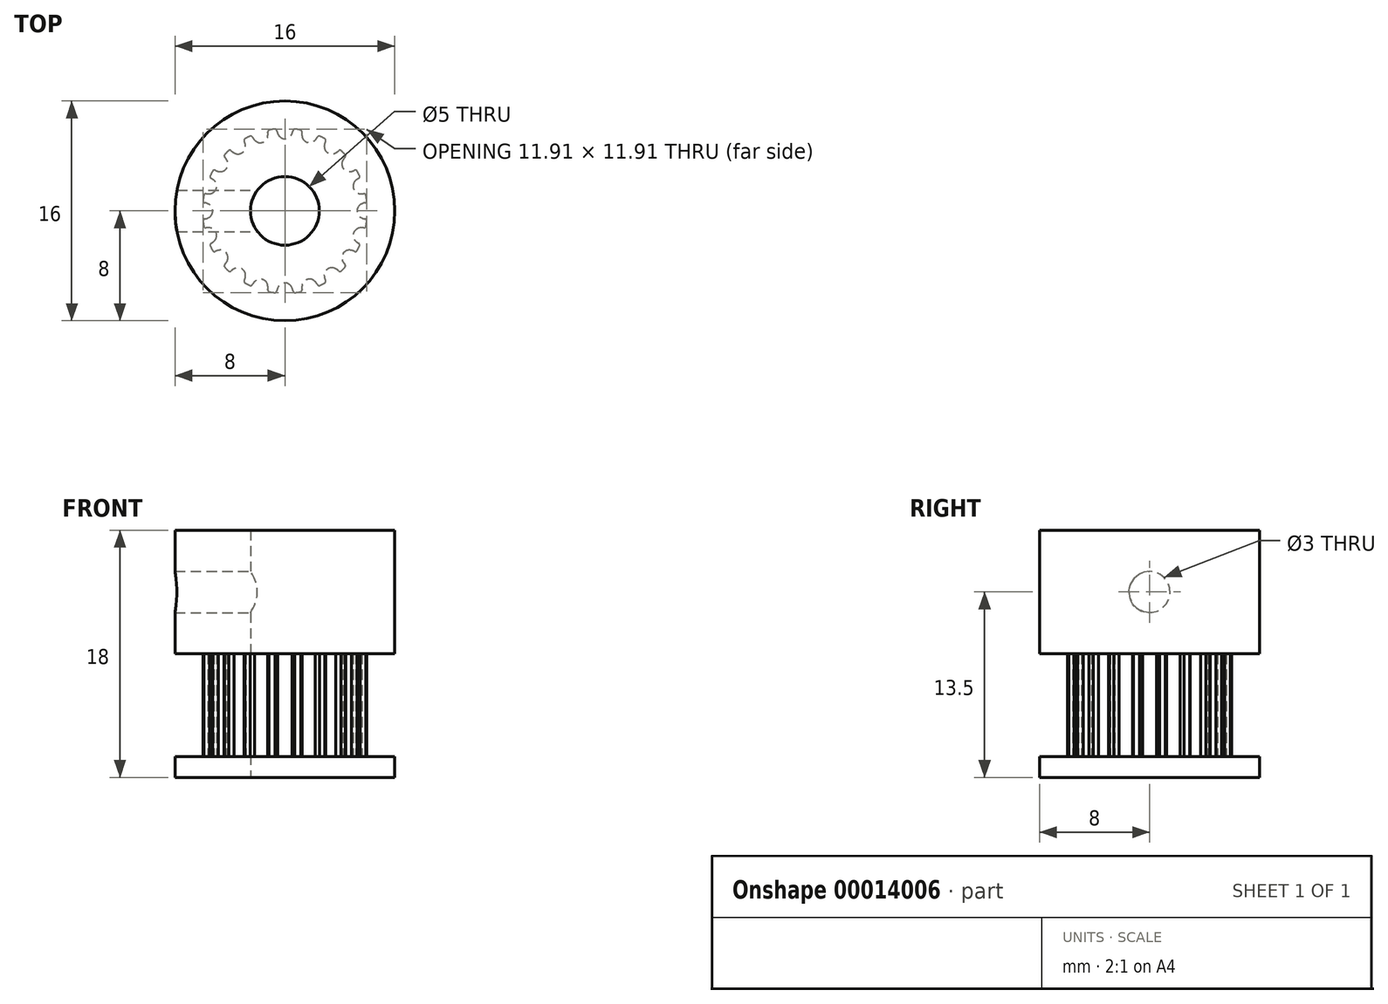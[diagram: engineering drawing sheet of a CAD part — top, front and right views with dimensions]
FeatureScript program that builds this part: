
annotation { "Feature Type Name" : "Feature", "Feature Type Description" : "" }
export const myFeature = defineFeature(function(context is Context, id is Id, definition is map)
    precondition{}
    {
        {
            var Q0;
            Q0=qCreatedBy(makeId("Top.planeOp"),FACE);
            var sketch = newSketch(context, id + "F0", { "sketchPlane" : qUnion([Q0])});
            skLineSegment(sketch, "E0", {"start": v(-19.17, 17.78) * mm, "end": v(-18.17, 17.78) * mm});
            skLineSegment(sketch, "E1", {"start": v(-18.17, 17.78) * mm, "end": v(-18.17, 18.4) * mm});
            skArc(sketch, "E2", {"start": v(-18.67, 18.85) * mm, "mid": v(-18.88, 19.07) * mm, "end": v(-19.17, 19.16) * mm});
            skArc(sketch, "E3", {"start": v(-18.58, 18.54) * mm, "mid": v(-18.61, 18.7) * mm, "end": v(-18.67, 18.85) * mm});
            skArc(sketch, "E4", {"start": v(-18.58, 18.54) * mm, "mid": v(-18.53, 18.44) * mm, "end": v(-18.43, 18.4) * mm});
            skLineSegment(sketch, "E5", {"start": v(-18.43, 18.4) * mm, "end": v(-18.17, 18.4) * mm});
            skArc(sketch, "E6.0.MirrorCS", {"start": v(-19.67, 18.85) * mm, "mid": v(-19.47, 19.07) * mm, "end": v(-19.17, 19.16) * mm});
            skArc(sketch, "E7.0.MirrorCS", {"start": v(-19.76, 18.54) * mm, "mid": v(-19.73, 18.7) * mm, "end": v(-19.67, 18.85) * mm});
            skArc(sketch, "E8.0.MirrorCS", {"start": v(-19.76, 18.54) * mm, "mid": v(-19.81, 18.44) * mm, "end": v(-19.91, 18.4) * mm});
            skLineSegment(sketch, "E9.0.MirrorCS", {"start": v(-19.91, 18.4) * mm, "end": v(-20.17, 18.4) * mm});
            skLineSegment(sketch, "E10.0.MirrorCS", {"start": v(-20.17, 17.78) * mm, "end": v(-20.17, 18.4) * mm});
            skLineSegment(sketch, "E11.0.MirrorCS", {"start": v(-19.17, 17.78) * mm, "end": v(-20.17, 17.78) * mm});
            skLineSegment(sketch, "E12.direction1", {"start": v(-20.17, 17.78) * mm, "end": v(-18.17, 17.78) * mm, "construction": true});
            skLineSegment(sketch, "E13", {"start": v(-20.17, 18.15) * mm, "end": v(-18.17, 18.15) * mm, "construction": true});
            skPoint(sketch, "E14", {"position": v(0, -5.25) * mm});
            skArc(sketch, "E15", {"start": v(0.51, -5.6) * mm, "mid": v(0, -5.25) * mm, "end": v(-0.51, -5.6) * mm});
            skArc(sketch, "E16", {"start": v(-0.51, -5.6) * mm, "mid": v(-0.56, -5.71) * mm, "end": v(-0.59, -5.83) * mm});
            skArc(sketch, "E17", {"start": v(0.59, -5.83) * mm, "mid": v(0.56, -5.71) * mm, "end": v(0.51, -5.6) * mm});
            skArc(sketch, "E18", {"start": v(0.72, -5.96) * mm, "mid": v(0.94, -5.93) * mm, "end": v(1.16, -5.89) * mm});
            skArc(sketch, "E19", {"start": v(0.59, -5.83) * mm, "mid": v(0.66, -5.94) * mm, "end": v(0.8, -5.95) * mm});
            skArc(sketch, "E20", {"start": v(-0.59, -5.83) * mm, "mid": v(-0.66, -5.94) * mm, "end": v(-0.8, -5.95) * mm});
            skArc(sketch, "E21.1.0", {"start": v(2.22, -5.16) * mm, "mid": v(1.62, -5) * mm, "end": v(1.24, -5.48) * mm});
            skPoint(sketch, "E21.1.1", {"position": v(1.62, -5) * mm});
            skArc(sketch, "E21.1.2", {"start": v(1.24, -5.48) * mm, "mid": v(1.23, -5.6) * mm, "end": v(1.24, -5.73) * mm});
            skArc(sketch, "E21.1.3", {"start": v(2.36, -5.37) * mm, "mid": v(2.47, -5.44) * mm, "end": v(2.6, -5.41) * mm});
            skArc(sketch, "E21.1.4", {"start": v(1.24, -5.73) * mm, "mid": v(1.2, -5.85) * mm, "end": v(1.08, -5.9) * mm});
            skArc(sketch, "E21.1.5", {"start": v(2.36, -5.37) * mm, "mid": v(2.3, -5.26) * mm, "end": v(2.22, -5.16) * mm});
            skArc(sketch, "E22.3.2.0", {"start": v(3.7, -4.22) * mm, "mid": v(3.09, -4.25) * mm, "end": v(2.87, -4.83) * mm});
            skPoint(sketch, "E22.4.2.0", {"position": v(3.09, -4.25) * mm});
            skArc(sketch, "E22.5.2.0", {"start": v(2.87, -4.83) * mm, "mid": v(2.9, -4.95) * mm, "end": v(2.95, -5.07) * mm});
            skArc(sketch, "E22.9.2.0", {"start": v(3.9, -4.37) * mm, "mid": v(4.03, -4.41) * mm, "end": v(4.14, -4.35) * mm});
            skArc(sketch, "E22.13.2.0", {"start": v(2.95, -5.07) * mm, "mid": v(2.95, -5.2) * mm, "end": v(2.85, -5.28) * mm});
            skArc(sketch, "E22.17.2.0", {"start": v(3.9, -4.37) * mm, "mid": v(3.81, -4.3) * mm, "end": v(3.7, -4.22) * mm});
            skArc(sketch, "E22.3.3.0", {"start": v(4.83, -2.87) * mm, "mid": v(4.25, -3.09) * mm, "end": v(4.22, -3.7) * mm});
            skPoint(sketch, "E22.4.3.0", {"position": v(4.25, -3.09) * mm});
            skArc(sketch, "E22.5.3.0", {"start": v(4.22, -3.7) * mm, "mid": v(4.3, -3.81) * mm, "end": v(4.37, -3.9) * mm});
            skArc(sketch, "E22.9.3.0", {"start": v(5.07, -2.95) * mm, "mid": v(5.2, -2.95) * mm, "end": v(5.28, -2.85) * mm});
            skArc(sketch, "E22.13.3.0", {"start": v(4.37, -3.9) * mm, "mid": v(4.41, -4.03) * mm, "end": v(4.35, -4.14) * mm});
            skArc(sketch, "E22.17.3.0", {"start": v(5.07, -2.95) * mm, "mid": v(4.95, -2.9) * mm, "end": v(4.83, -2.87) * mm});
            skArc(sketch, "E22.3.4.0", {"start": v(5.48, -1.24) * mm, "mid": v(5, -1.62) * mm, "end": v(5.16, -2.22) * mm});
            skPoint(sketch, "E22.4.4.0", {"position": v(5, -1.62) * mm});
            skArc(sketch, "E22.5.4.0", {"start": v(5.16, -2.22) * mm, "mid": v(5.26, -2.3) * mm, "end": v(5.37, -2.36) * mm});
            skArc(sketch, "E22.9.4.0", {"start": v(5.73, -1.24) * mm, "mid": v(5.85, -1.2) * mm, "end": v(5.9, -1.08) * mm});
            skArc(sketch, "E22.13.4.0", {"start": v(5.37, -2.36) * mm, "mid": v(5.44, -2.47) * mm, "end": v(5.41, -2.6) * mm});
            skArc(sketch, "E22.17.4.0", {"start": v(5.73, -1.24) * mm, "mid": v(5.6, -1.23) * mm, "end": v(5.48, -1.24) * mm});
            skArc(sketch, "E22.3.5.0", {"start": v(5.6, 0.51) * mm, "mid": v(5.25, 0) * mm, "end": v(5.6, -0.51) * mm});
            skPoint(sketch, "E22.4.5.0", {"position": v(5.25, 0) * mm});
            skArc(sketch, "E22.5.5.0", {"start": v(5.6, -0.51) * mm, "mid": v(5.71, -0.56) * mm, "end": v(5.83, -0.59) * mm});
            skArc(sketch, "E22.9.5.0", {"start": v(5.83, 0.59) * mm, "mid": v(5.94, 0.66) * mm, "end": v(5.95, 0.8) * mm});
            skArc(sketch, "E22.13.5.0", {"start": v(5.83, -0.59) * mm, "mid": v(5.94, -0.66) * mm, "end": v(5.95, -0.8) * mm});
            skArc(sketch, "E22.17.5.0", {"start": v(5.83, 0.59) * mm, "mid": v(5.71, 0.56) * mm, "end": v(5.6, 0.51) * mm});
            skArc(sketch, "E22.3.6.0", {"start": v(5.16, 2.22) * mm, "mid": v(5, 1.62) * mm, "end": v(5.48, 1.24) * mm});
            skPoint(sketch, "E22.4.6.0", {"position": v(5, 1.62) * mm});
            skArc(sketch, "E22.5.6.0", {"start": v(5.48, 1.24) * mm, "mid": v(5.6, 1.23) * mm, "end": v(5.73, 1.24) * mm});
            skArc(sketch, "E22.9.6.0", {"start": v(5.37, 2.36) * mm, "mid": v(5.44, 2.47) * mm, "end": v(5.41, 2.6) * mm});
            skArc(sketch, "E22.13.6.0", {"start": v(5.73, 1.24) * mm, "mid": v(5.85, 1.2) * mm, "end": v(5.9, 1.08) * mm});
            skArc(sketch, "E22.17.6.0", {"start": v(5.37, 2.36) * mm, "mid": v(5.26, 2.3) * mm, "end": v(5.16, 2.22) * mm});
            skArc(sketch, "E22.3.7.0", {"start": v(4.22, 3.7) * mm, "mid": v(4.25, 3.09) * mm, "end": v(4.83, 2.87) * mm});
            skPoint(sketch, "E22.4.7.0", {"position": v(4.25, 3.09) * mm});
            skArc(sketch, "E22.5.7.0", {"start": v(4.83, 2.87) * mm, "mid": v(4.95, 2.9) * mm, "end": v(5.07, 2.95) * mm});
            skArc(sketch, "E22.9.7.0", {"start": v(4.37, 3.9) * mm, "mid": v(4.41, 4.03) * mm, "end": v(4.35, 4.14) * mm});
            skArc(sketch, "E22.13.7.0", {"start": v(5.07, 2.95) * mm, "mid": v(5.2, 2.95) * mm, "end": v(5.28, 2.85) * mm});
            skArc(sketch, "E22.17.7.0", {"start": v(4.37, 3.9) * mm, "mid": v(4.3, 3.81) * mm, "end": v(4.22, 3.7) * mm});
            skArc(sketch, "E22.3.8.0", {"start": v(2.87, 4.83) * mm, "mid": v(3.09, 4.25) * mm, "end": v(3.7, 4.22) * mm});
            skPoint(sketch, "E22.4.8.0", {"position": v(3.09, 4.25) * mm});
            skArc(sketch, "E22.5.8.0", {"start": v(3.7, 4.22) * mm, "mid": v(3.81, 4.3) * mm, "end": v(3.9, 4.37) * mm});
            skArc(sketch, "E22.9.8.0", {"start": v(2.95, 5.07) * mm, "mid": v(2.95, 5.2) * mm, "end": v(2.85, 5.28) * mm});
            skArc(sketch, "E22.13.8.0", {"start": v(3.9, 4.37) * mm, "mid": v(4.03, 4.41) * mm, "end": v(4.14, 4.35) * mm});
            skArc(sketch, "E22.17.8.0", {"start": v(2.95, 5.07) * mm, "mid": v(2.9, 4.95) * mm, "end": v(2.87, 4.83) * mm});
            skArc(sketch, "E22.3.9.0", {"start": v(1.24, 5.48) * mm, "mid": v(1.62, 5) * mm, "end": v(2.22, 5.16) * mm});
            skPoint(sketch, "E22.4.9.0", {"position": v(1.62, 5) * mm});
            skArc(sketch, "E22.5.9.0", {"start": v(2.22, 5.16) * mm, "mid": v(2.3, 5.26) * mm, "end": v(2.36, 5.37) * mm});
            skArc(sketch, "E22.9.9.0", {"start": v(1.24, 5.73) * mm, "mid": v(1.2, 5.85) * mm, "end": v(1.08, 5.9) * mm});
            skArc(sketch, "E22.13.9.0", {"start": v(2.36, 5.37) * mm, "mid": v(2.47, 5.44) * mm, "end": v(2.6, 5.41) * mm});
            skArc(sketch, "E22.17.9.0", {"start": v(1.24, 5.73) * mm, "mid": v(1.23, 5.6) * mm, "end": v(1.24, 5.48) * mm});
            skArc(sketch, "E22.3.10.0", {"start": v(-0.51, 5.6) * mm, "mid": v(0, 5.25) * mm, "end": v(0.51, 5.6) * mm});
            skPoint(sketch, "E22.4.10.0", {"position": v(0, 5.25) * mm});
            skArc(sketch, "E22.5.10.0", {"start": v(0.51, 5.6) * mm, "mid": v(0.56, 5.71) * mm, "end": v(0.59, 5.83) * mm});
            skArc(sketch, "E22.9.10.0", {"start": v(-0.59, 5.83) * mm, "mid": v(-0.66, 5.94) * mm, "end": v(-0.8, 5.95) * mm});
            skArc(sketch, "E22.13.10.0", {"start": v(0.59, 5.83) * mm, "mid": v(0.66, 5.94) * mm, "end": v(0.8, 5.95) * mm});
            skArc(sketch, "E22.17.10.0", {"start": v(-0.59, 5.83) * mm, "mid": v(-0.56, 5.71) * mm, "end": v(-0.51, 5.6) * mm});
            skArc(sketch, "E22.3.11.0", {"start": v(-2.22, 5.16) * mm, "mid": v(-1.62, 5) * mm, "end": v(-1.24, 5.48) * mm});
            skPoint(sketch, "E22.4.11.0", {"position": v(-1.62, 5) * mm});
            skArc(sketch, "E22.5.11.0", {"start": v(-1.24, 5.48) * mm, "mid": v(-1.23, 5.6) * mm, "end": v(-1.24, 5.73) * mm});
            skArc(sketch, "E22.9.11.0", {"start": v(-2.36, 5.37) * mm, "mid": v(-2.47, 5.44) * mm, "end": v(-2.6, 5.41) * mm});
            skArc(sketch, "E22.13.11.0", {"start": v(-1.24, 5.73) * mm, "mid": v(-1.2, 5.85) * mm, "end": v(-1.08, 5.9) * mm});
            skArc(sketch, "E22.17.11.0", {"start": v(-2.36, 5.37) * mm, "mid": v(-2.3, 5.26) * mm, "end": v(-2.22, 5.16) * mm});
            skArc(sketch, "E22.3.12.0", {"start": v(-3.7, 4.22) * mm, "mid": v(-3.09, 4.25) * mm, "end": v(-2.87, 4.83) * mm});
            skPoint(sketch, "E22.4.12.0", {"position": v(-3.09, 4.25) * mm});
            skArc(sketch, "E22.5.12.0", {"start": v(-2.87, 4.83) * mm, "mid": v(-2.9, 4.95) * mm, "end": v(-2.95, 5.07) * mm});
            skArc(sketch, "E22.9.12.0", {"start": v(-3.9, 4.37) * mm, "mid": v(-4.03, 4.41) * mm, "end": v(-4.14, 4.35) * mm});
            skArc(sketch, "E22.13.12.0", {"start": v(-2.95, 5.07) * mm, "mid": v(-2.95, 5.2) * mm, "end": v(-2.85, 5.28) * mm});
            skArc(sketch, "E22.17.12.0", {"start": v(-3.9, 4.37) * mm, "mid": v(-3.81, 4.3) * mm, "end": v(-3.7, 4.22) * mm});
            skArc(sketch, "E22.3.13.0", {"start": v(-4.83, 2.87) * mm, "mid": v(-4.25, 3.09) * mm, "end": v(-4.22, 3.7) * mm});
            skPoint(sketch, "E22.4.13.0", {"position": v(-4.25, 3.09) * mm});
            skArc(sketch, "E22.5.13.0", {"start": v(-4.22, 3.7) * mm, "mid": v(-4.3, 3.81) * mm, "end": v(-4.37, 3.9) * mm});
            skArc(sketch, "E22.9.13.0", {"start": v(-5.07, 2.95) * mm, "mid": v(-5.2, 2.95) * mm, "end": v(-5.28, 2.85) * mm});
            skArc(sketch, "E22.13.13.0", {"start": v(-4.37, 3.9) * mm, "mid": v(-4.41, 4.03) * mm, "end": v(-4.35, 4.14) * mm});
            skArc(sketch, "E22.17.13.0", {"start": v(-5.07, 2.95) * mm, "mid": v(-4.95, 2.9) * mm, "end": v(-4.83, 2.87) * mm});
            skArc(sketch, "E22.3.14.0", {"start": v(-5.48, 1.24) * mm, "mid": v(-5, 1.62) * mm, "end": v(-5.16, 2.22) * mm});
            skPoint(sketch, "E22.4.14.0", {"position": v(-5, 1.62) * mm});
            skArc(sketch, "E22.5.14.0", {"start": v(-5.16, 2.22) * mm, "mid": v(-5.26, 2.3) * mm, "end": v(-5.37, 2.36) * mm});
            skArc(sketch, "E22.9.14.0", {"start": v(-5.73, 1.24) * mm, "mid": v(-5.85, 1.2) * mm, "end": v(-5.9, 1.08) * mm});
            skArc(sketch, "E22.13.14.0", {"start": v(-5.37, 2.36) * mm, "mid": v(-5.44, 2.47) * mm, "end": v(-5.41, 2.6) * mm});
            skArc(sketch, "E22.17.14.0", {"start": v(-5.73, 1.24) * mm, "mid": v(-5.6, 1.23) * mm, "end": v(-5.48, 1.24) * mm});
            skArc(sketch, "E22.3.15.0", {"start": v(-5.6, -0.51) * mm, "mid": v(-5.25, 0) * mm, "end": v(-5.6, 0.51) * mm});
            skPoint(sketch, "E22.4.15.0", {"position": v(-5.25, 0) * mm});
            skArc(sketch, "E22.5.15.0", {"start": v(-5.6, 0.51) * mm, "mid": v(-5.71, 0.56) * mm, "end": v(-5.83, 0.59) * mm});
            skArc(sketch, "E22.9.15.0", {"start": v(-5.83, -0.59) * mm, "mid": v(-5.94, -0.66) * mm, "end": v(-5.95, -0.8) * mm});
            skArc(sketch, "E22.13.15.0", {"start": v(-5.83, 0.59) * mm, "mid": v(-5.94, 0.66) * mm, "end": v(-5.95, 0.8) * mm});
            skArc(sketch, "E22.17.15.0", {"start": v(-5.83, -0.59) * mm, "mid": v(-5.71, -0.56) * mm, "end": v(-5.6, -0.51) * mm});
            skArc(sketch, "E22.3.16.0", {"start": v(-5.16, -2.22) * mm, "mid": v(-5, -1.62) * mm, "end": v(-5.48, -1.24) * mm});
            skPoint(sketch, "E22.4.16.0", {"position": v(-5, -1.62) * mm});
            skArc(sketch, "E22.5.16.0", {"start": v(-5.48, -1.24) * mm, "mid": v(-5.6, -1.23) * mm, "end": v(-5.73, -1.24) * mm});
            skArc(sketch, "E22.9.16.0", {"start": v(-5.37, -2.36) * mm, "mid": v(-5.44, -2.47) * mm, "end": v(-5.41, -2.6) * mm});
            skArc(sketch, "E22.13.16.0", {"start": v(-5.73, -1.24) * mm, "mid": v(-5.85, -1.2) * mm, "end": v(-5.9, -1.08) * mm});
            skArc(sketch, "E22.17.16.0", {"start": v(-5.37, -2.36) * mm, "mid": v(-5.26, -2.3) * mm, "end": v(-5.16, -2.22) * mm});
            skArc(sketch, "E22.3.17.0", {"start": v(-4.22, -3.7) * mm, "mid": v(-4.25, -3.09) * mm, "end": v(-4.83, -2.87) * mm});
            skPoint(sketch, "E22.4.17.0", {"position": v(-4.25, -3.09) * mm});
            skArc(sketch, "E22.5.17.0", {"start": v(-4.83, -2.87) * mm, "mid": v(-4.95, -2.9) * mm, "end": v(-5.07, -2.95) * mm});
            skArc(sketch, "E22.9.17.0", {"start": v(-4.37, -3.9) * mm, "mid": v(-4.41, -4.03) * mm, "end": v(-4.35, -4.14) * mm});
            skArc(sketch, "E22.13.17.0", {"start": v(-5.07, -2.95) * mm, "mid": v(-5.2, -2.95) * mm, "end": v(-5.28, -2.85) * mm});
            skArc(sketch, "E22.17.17.0", {"start": v(-4.37, -3.9) * mm, "mid": v(-4.3, -3.81) * mm, "end": v(-4.22, -3.7) * mm});
            skArc(sketch, "E22.3.18.0", {"start": v(-2.87, -4.83) * mm, "mid": v(-3.09, -4.25) * mm, "end": v(-3.7, -4.22) * mm});
            skPoint(sketch, "E22.4.18.0", {"position": v(-3.09, -4.25) * mm});
            skArc(sketch, "E22.5.18.0", {"start": v(-3.7, -4.22) * mm, "mid": v(-3.81, -4.3) * mm, "end": v(-3.9, -4.37) * mm});
            skArc(sketch, "E22.9.18.0", {"start": v(-2.95, -5.07) * mm, "mid": v(-2.95, -5.2) * mm, "end": v(-2.85, -5.28) * mm});
            skArc(sketch, "E22.13.18.0", {"start": v(-3.9, -4.37) * mm, "mid": v(-4.03, -4.41) * mm, "end": v(-4.14, -4.35) * mm});
            skArc(sketch, "E22.17.18.0", {"start": v(-2.95, -5.07) * mm, "mid": v(-2.9, -4.95) * mm, "end": v(-2.87, -4.83) * mm});
            skArc(sketch, "E22.3.19.0", {"start": v(-1.24, -5.48) * mm, "mid": v(-1.62, -5) * mm, "end": v(-2.22, -5.16) * mm});
            skPoint(sketch, "E22.4.19.0", {"position": v(-1.62, -5) * mm});
            skArc(sketch, "E22.5.19.0", {"start": v(-2.22, -5.16) * mm, "mid": v(-2.3, -5.26) * mm, "end": v(-2.36, -5.37) * mm});
            skArc(sketch, "E22.9.19.0", {"start": v(-1.24, -5.73) * mm, "mid": v(-1.2, -5.85) * mm, "end": v(-1.08, -5.9) * mm});
            skArc(sketch, "E22.13.19.0", {"start": v(-2.36, -5.37) * mm, "mid": v(-2.47, -5.44) * mm, "end": v(-2.6, -5.41) * mm});
            skArc(sketch, "E22.17.19.0", {"start": v(-1.24, -5.73) * mm, "mid": v(-1.23, -5.6) * mm, "end": v(-1.24, -5.48) * mm});
            skArc(sketch, "E23.trimOffspring", {"start": v(2.52, -5.44) * mm, "mid": v(2.72, -5.35) * mm, "end": v(2.92, -5.24) * mm});
            skArc(sketch, "E24.trimOffspring", {"start": v(4.08, -4.4) * mm, "mid": v(4.24, -4.24) * mm, "end": v(4.4, -4.08) * mm});
            skArc(sketch, "E25.trimOffspring", {"start": v(5.24, -2.92) * mm, "mid": v(5.33, -2.76) * mm, "end": v(5.41, -2.6) * mm});
            skArc(sketch, "E26.trimOffspring", {"start": v(5.89, -1.16) * mm, "mid": v(5.93, -0.94) * mm, "end": v(5.96, -0.72) * mm});
            skArc(sketch, "E27.trimOffspring", {"start": v(5.44, 2.52) * mm, "mid": v(5.35, 2.72) * mm, "end": v(5.24, 2.92) * mm});
            skArc(sketch, "E28.trimOffspring", {"start": v(4.4, 4.08) * mm, "mid": v(4.24, 4.24) * mm, "end": v(4.08, 4.4) * mm});
            skArc(sketch, "E29.trimOffspring", {"start": v(5.96, 0.72) * mm, "mid": v(5.93, 0.94) * mm, "end": v(5.89, 1.16) * mm});
            skArc(sketch, "E30.trimOffspring", {"start": v(2.92, 5.24) * mm, "mid": v(2.72, 5.35) * mm, "end": v(2.52, 5.44) * mm});
            skArc(sketch, "E31.trimOffspring", {"start": v(1.16, 5.89) * mm, "mid": v(0.94, 5.93) * mm, "end": v(0.72, 5.96) * mm});
            skArc(sketch, "E32.trimOffspring", {"start": v(-0.72, 5.96) * mm, "mid": v(-0.94, 5.93) * mm, "end": v(-1.16, 5.89) * mm});
            skArc(sketch, "E33.trimOffspring", {"start": v(-2.52, 5.44) * mm, "mid": v(-2.72, 5.35) * mm, "end": v(-2.92, 5.24) * mm});
            skArc(sketch, "E34.trimOffspring", {"start": v(-4.08, 4.4) * mm, "mid": v(-4.24, 4.24) * mm, "end": v(-4.4, 4.08) * mm});
            skArc(sketch, "E35.trimOffspring", {"start": v(-5.24, 2.92) * mm, "mid": v(-5.35, 2.72) * mm, "end": v(-5.44, 2.52) * mm});
            skArc(sketch, "E36.trimOffspring", {"start": v(-5.89, 1.16) * mm, "mid": v(-5.93, 0.94) * mm, "end": v(-5.96, 0.72) * mm});
            skArc(sketch, "E37.trimOffspring", {"start": v(-5.96, -0.72) * mm, "mid": v(-5.93, -0.94) * mm, "end": v(-5.89, -1.16) * mm});
            skArc(sketch, "E38.trimOffspring", {"start": v(-5.44, -2.52) * mm, "mid": v(-5.35, -2.72) * mm, "end": v(-5.24, -2.92) * mm});
            skArc(sketch, "E39.trimOffspring", {"start": v(-4.4, -4.08) * mm, "mid": v(-4.24, -4.24) * mm, "end": v(-4.08, -4.4) * mm});
            skArc(sketch, "E40.trimOffspring", {"start": v(-2.92, -5.24) * mm, "mid": v(-2.72, -5.35) * mm, "end": v(-2.52, -5.44) * mm});
            skArc(sketch, "E41.trimOffspring", {"start": v(-1.16, -5.89) * mm, "mid": v(-0.94, -5.93) * mm, "end": v(-0.72, -5.96) * mm});
            skSolve(sketch);
        }
        {
            var Q0;
            Q0=makeQuery(id+"F0.imprint","IMPRINT",FACE,{"disambiguationData":[TD([[makeQuery(id+"F0.imprint","IMPRINT",EDGE,{"derivedFrom":sQuery(id+"F0.wireOp",EDGE,"E15")}),-1.0]])]});
            extrude(context, id + "F1", {"entities" : qUnion([Q0]), "depth" : 7.5 * mm});
        }
        {
            var Q0;
            Q0=makeQuery(id+"F1.opExtrude","CAP_FACE",FACE,{"disambiguationData":[OSD([sQuery(id+"F0.wireOp",EDGE,"E15"),sQuery(id+"F0.wireOp",EDGE,"E16"),sQuery(id+"F0.wireOp",EDGE,"E17"),sQuery(id+"F0.wireOp",EDGE,"E18"),sQuery(id+"F0.wireOp",EDGE,"E19"),sQuery(id+"F0.wireOp",EDGE,"E20"),sQuery(id+"F0.wireOp",EDGE,"E21.1.0"),sQuery(id+"F0.wireOp",EDGE,"E21.1.2"),sQuery(id+"F0.wireOp",EDGE,"E21.1.3"),sQuery(id+"F0.wireOp",EDGE,"E21.1.4"),sQuery(id+"F0.wireOp",EDGE,"E21.1.5"),sQuery(id+"F0.wireOp",EDGE,"E22.3.2.0"),sQuery(id+"F0.wireOp",EDGE,"E22.5.2.0"),sQuery(id+"F0.wireOp",EDGE,"E22.9.2.0"),sQuery(id+"F0.wireOp",EDGE,"E22.13.2.0"),sQuery(id+"F0.wireOp",EDGE,"E22.17.2.0"),sQuery(id+"F0.wireOp",EDGE,"E22.3.3.0"),sQuery(id+"F0.wireOp",EDGE,"E22.5.3.0"),sQuery(id+"F0.wireOp",EDGE,"E22.9.3.0"),sQuery(id+"F0.wireOp",EDGE,"E22.13.3.0"),sQuery(id+"F0.wireOp",EDGE,"E22.17.3.0"),sQuery(id+"F0.wireOp",EDGE,"E22.3.4.0"),sQuery(id+"F0.wireOp",EDGE,"E22.5.4.0"),sQuery(id+"F0.wireOp",EDGE,"E22.9.4.0"),sQuery(id+"F0.wireOp",EDGE,"E22.13.4.0"),sQuery(id+"F0.wireOp",EDGE,"E22.17.4.0"),sQuery(id+"F0.wireOp",EDGE,"E22.3.5.0"),sQuery(id+"F0.wireOp",EDGE,"E22.5.5.0"),sQuery(id+"F0.wireOp",EDGE,"E22.9.5.0"),sQuery(id+"F0.wireOp",EDGE,"E22.13.5.0"),sQuery(id+"F0.wireOp",EDGE,"E22.17.5.0"),sQuery(id+"F0.wireOp",EDGE,"E22.3.6.0"),sQuery(id+"F0.wireOp",EDGE,"E22.5.6.0"),sQuery(id+"F0.wireOp",EDGE,"E22.9.6.0"),sQuery(id+"F0.wireOp",EDGE,"E22.13.6.0"),sQuery(id+"F0.wireOp",EDGE,"E22.17.6.0"),sQuery(id+"F0.wireOp",EDGE,"E22.3.7.0"),sQuery(id+"F0.wireOp",EDGE,"E22.5.7.0"),sQuery(id+"F0.wireOp",EDGE,"E22.9.7.0"),sQuery(id+"F0.wireOp",EDGE,"E22.13.7.0"),sQuery(id+"F0.wireOp",EDGE,"E22.17.7.0"),sQuery(id+"F0.wireOp",EDGE,"E22.3.8.0"),sQuery(id+"F0.wireOp",EDGE,"E22.5.8.0"),sQuery(id+"F0.wireOp",EDGE,"E22.9.8.0"),sQuery(id+"F0.wireOp",EDGE,"E22.13.8.0"),sQuery(id+"F0.wireOp",EDGE,"E22.17.8.0"),sQuery(id+"F0.wireOp",EDGE,"E22.3.9.0"),sQuery(id+"F0.wireOp",EDGE,"E22.5.9.0"),sQuery(id+"F0.wireOp",EDGE,"E22.9.9.0"),sQuery(id+"F0.wireOp",EDGE,"E22.13.9.0"),sQuery(id+"F0.wireOp",EDGE,"E22.17.9.0"),sQuery(id+"F0.wireOp",EDGE,"E22.3.10.0"),sQuery(id+"F0.wireOp",EDGE,"E22.5.10.0"),sQuery(id+"F0.wireOp",EDGE,"E22.9.10.0"),sQuery(id+"F0.wireOp",EDGE,"E22.13.10.0"),sQuery(id+"F0.wireOp",EDGE,"E22.17.10.0"),sQuery(id+"F0.wireOp",EDGE,"E22.3.11.0"),sQuery(id+"F0.wireOp",EDGE,"E22.5.11.0"),sQuery(id+"F0.wireOp",EDGE,"E22.9.11.0"),sQuery(id+"F0.wireOp",EDGE,"E22.13.11.0"),sQuery(id+"F0.wireOp",EDGE,"E22.17.11.0"),sQuery(id+"F0.wireOp",EDGE,"E22.3.12.0"),sQuery(id+"F0.wireOp",EDGE,"E22.5.12.0"),sQuery(id+"F0.wireOp",EDGE,"E22.9.12.0"),sQuery(id+"F0.wireOp",EDGE,"E22.13.12.0"),sQuery(id+"F0.wireOp",EDGE,"E22.17.12.0"),sQuery(id+"F0.wireOp",EDGE,"E22.3.13.0"),sQuery(id+"F0.wireOp",EDGE,"E22.5.13.0"),sQuery(id+"F0.wireOp",EDGE,"E22.9.13.0"),sQuery(id+"F0.wireOp",EDGE,"E22.13.13.0"),sQuery(id+"F0.wireOp",EDGE,"E22.17.13.0"),sQuery(id+"F0.wireOp",EDGE,"E22.3.14.0"),sQuery(id+"F0.wireOp",EDGE,"E22.5.14.0"),sQuery(id+"F0.wireOp",EDGE,"E22.9.14.0"),sQuery(id+"F0.wireOp",EDGE,"E22.13.14.0"),sQuery(id+"F0.wireOp",EDGE,"E22.17.14.0"),sQuery(id+"F0.wireOp",EDGE,"E22.3.15.0"),sQuery(id+"F0.wireOp",EDGE,"E22.5.15.0"),sQuery(id+"F0.wireOp",EDGE,"E22.9.15.0"),sQuery(id+"F0.wireOp",EDGE,"E22.13.15.0"),sQuery(id+"F0.wireOp",EDGE,"E22.17.15.0"),sQuery(id+"F0.wireOp",EDGE,"E22.3.16.0"),sQuery(id+"F0.wireOp",EDGE,"E22.5.16.0"),sQuery(id+"F0.wireOp",EDGE,"E22.9.16.0"),sQuery(id+"F0.wireOp",EDGE,"E22.13.16.0"),sQuery(id+"F0.wireOp",EDGE,"E22.17.16.0"),sQuery(id+"F0.wireOp",EDGE,"E22.3.17.0"),sQuery(id+"F0.wireOp",EDGE,"E22.5.17.0"),sQuery(id+"F0.wireOp",EDGE,"E22.9.17.0"),sQuery(id+"F0.wireOp",EDGE,"E22.13.17.0"),sQuery(id+"F0.wireOp",EDGE,"E22.17.17.0"),sQuery(id+"F0.wireOp",EDGE,"E22.3.18.0"),sQuery(id+"F0.wireOp",EDGE,"E22.5.18.0"),sQuery(id+"F0.wireOp",EDGE,"E22.9.18.0"),sQuery(id+"F0.wireOp",EDGE,"E22.13.18.0"),sQuery(id+"F0.wireOp",EDGE,"E22.17.18.0"),sQuery(id+"F0.wireOp",EDGE,"E22.3.19.0"),sQuery(id+"F0.wireOp",EDGE,"E22.5.19.0"),sQuery(id+"F0.wireOp",EDGE,"E22.9.19.0"),sQuery(id+"F0.wireOp",EDGE,"E22.13.19.0"),sQuery(id+"F0.wireOp",EDGE,"E22.17.19.0"),sQuery(id+"F0.wireOp",EDGE,"E23.trimOffspring"),sQuery(id+"F0.wireOp",EDGE,"E24.trimOffspring"),sQuery(id+"F0.wireOp",EDGE,"E25.trimOffspring"),sQuery(id+"F0.wireOp",EDGE,"E26.trimOffspring"),sQuery(id+"F0.wireOp",EDGE,"E27.trimOffspring"),sQuery(id+"F0.wireOp",EDGE,"E28.trimOffspring"),sQuery(id+"F0.wireOp",EDGE,"E29.trimOffspring"),sQuery(id+"F0.wireOp",EDGE,"E30.trimOffspring"),sQuery(id+"F0.wireOp",EDGE,"E31.trimOffspring"),sQuery(id+"F0.wireOp",EDGE,"E32.trimOffspring"),sQuery(id+"F0.wireOp",EDGE,"E33.trimOffspring"),sQuery(id+"F0.wireOp",EDGE,"E34.trimOffspring"),sQuery(id+"F0.wireOp",EDGE,"E35.trimOffspring"),sQuery(id+"F0.wireOp",EDGE,"E36.trimOffspring"),sQuery(id+"F0.wireOp",EDGE,"E37.trimOffspring"),sQuery(id+"F0.wireOp",EDGE,"E38.trimOffspring"),sQuery(id+"F0.wireOp",EDGE,"E39.trimOffspring"),sQuery(id+"F0.wireOp",EDGE,"E40.trimOffspring"),sQuery(id+"F0.wireOp",EDGE,"E41.trimOffspring")])],"isStart":false});
            var sketch = newSketch(context, id + "F2", { "sketchPlane" : qUnion([Q0])});
            skCircle(sketch, "E42", {"center": v(0, 0) * mm, "radius": 8 * mm});
            skSolve(sketch);
        }
        {
            var Q0;
            Q0=qSketchRegion(id+"F2",true);
            extrude(context, id + "F3", {"entities" : qUnion([Q0]), "operationType" : NewBodyOperationType.ADD, "depth" : 9 * mm});
        }
        {
            var Q0;
            Q0=makeQuery(id+"F1.opExtrude","CAP_FACE",FACE,{"disambiguationData":[OSD([sQuery(id+"F0.wireOp",EDGE,"E15"),sQuery(id+"F0.wireOp",EDGE,"E16"),sQuery(id+"F0.wireOp",EDGE,"E17"),sQuery(id+"F0.wireOp",EDGE,"E18"),sQuery(id+"F0.wireOp",EDGE,"E19"),sQuery(id+"F0.wireOp",EDGE,"E20"),sQuery(id+"F0.wireOp",EDGE,"E21.1.0"),sQuery(id+"F0.wireOp",EDGE,"E21.1.2"),sQuery(id+"F0.wireOp",EDGE,"E21.1.3"),sQuery(id+"F0.wireOp",EDGE,"E21.1.4"),sQuery(id+"F0.wireOp",EDGE,"E21.1.5"),sQuery(id+"F0.wireOp",EDGE,"E22.3.2.0"),sQuery(id+"F0.wireOp",EDGE,"E22.5.2.0"),sQuery(id+"F0.wireOp",EDGE,"E22.9.2.0"),sQuery(id+"F0.wireOp",EDGE,"E22.13.2.0"),sQuery(id+"F0.wireOp",EDGE,"E22.17.2.0"),sQuery(id+"F0.wireOp",EDGE,"E22.3.3.0"),sQuery(id+"F0.wireOp",EDGE,"E22.5.3.0"),sQuery(id+"F0.wireOp",EDGE,"E22.9.3.0"),sQuery(id+"F0.wireOp",EDGE,"E22.13.3.0"),sQuery(id+"F0.wireOp",EDGE,"E22.17.3.0"),sQuery(id+"F0.wireOp",EDGE,"E22.3.4.0"),sQuery(id+"F0.wireOp",EDGE,"E22.5.4.0"),sQuery(id+"F0.wireOp",EDGE,"E22.9.4.0"),sQuery(id+"F0.wireOp",EDGE,"E22.13.4.0"),sQuery(id+"F0.wireOp",EDGE,"E22.17.4.0"),sQuery(id+"F0.wireOp",EDGE,"E22.3.5.0"),sQuery(id+"F0.wireOp",EDGE,"E22.5.5.0"),sQuery(id+"F0.wireOp",EDGE,"E22.9.5.0"),sQuery(id+"F0.wireOp",EDGE,"E22.13.5.0"),sQuery(id+"F0.wireOp",EDGE,"E22.17.5.0"),sQuery(id+"F0.wireOp",EDGE,"E22.3.6.0"),sQuery(id+"F0.wireOp",EDGE,"E22.5.6.0"),sQuery(id+"F0.wireOp",EDGE,"E22.9.6.0"),sQuery(id+"F0.wireOp",EDGE,"E22.13.6.0"),sQuery(id+"F0.wireOp",EDGE,"E22.17.6.0"),sQuery(id+"F0.wireOp",EDGE,"E22.3.7.0"),sQuery(id+"F0.wireOp",EDGE,"E22.5.7.0"),sQuery(id+"F0.wireOp",EDGE,"E22.9.7.0"),sQuery(id+"F0.wireOp",EDGE,"E22.13.7.0"),sQuery(id+"F0.wireOp",EDGE,"E22.17.7.0"),sQuery(id+"F0.wireOp",EDGE,"E22.3.8.0"),sQuery(id+"F0.wireOp",EDGE,"E22.5.8.0"),sQuery(id+"F0.wireOp",EDGE,"E22.9.8.0"),sQuery(id+"F0.wireOp",EDGE,"E22.13.8.0"),sQuery(id+"F0.wireOp",EDGE,"E22.17.8.0"),sQuery(id+"F0.wireOp",EDGE,"E22.3.9.0"),sQuery(id+"F0.wireOp",EDGE,"E22.5.9.0"),sQuery(id+"F0.wireOp",EDGE,"E22.9.9.0"),sQuery(id+"F0.wireOp",EDGE,"E22.13.9.0"),sQuery(id+"F0.wireOp",EDGE,"E22.17.9.0"),sQuery(id+"F0.wireOp",EDGE,"E22.3.10.0"),sQuery(id+"F0.wireOp",EDGE,"E22.5.10.0"),sQuery(id+"F0.wireOp",EDGE,"E22.9.10.0"),sQuery(id+"F0.wireOp",EDGE,"E22.13.10.0"),sQuery(id+"F0.wireOp",EDGE,"E22.17.10.0"),sQuery(id+"F0.wireOp",EDGE,"E22.3.11.0"),sQuery(id+"F0.wireOp",EDGE,"E22.5.11.0"),sQuery(id+"F0.wireOp",EDGE,"E22.9.11.0"),sQuery(id+"F0.wireOp",EDGE,"E22.13.11.0"),sQuery(id+"F0.wireOp",EDGE,"E22.17.11.0"),sQuery(id+"F0.wireOp",EDGE,"E22.3.12.0"),sQuery(id+"F0.wireOp",EDGE,"E22.5.12.0"),sQuery(id+"F0.wireOp",EDGE,"E22.9.12.0"),sQuery(id+"F0.wireOp",EDGE,"E22.13.12.0"),sQuery(id+"F0.wireOp",EDGE,"E22.17.12.0"),sQuery(id+"F0.wireOp",EDGE,"E22.3.13.0"),sQuery(id+"F0.wireOp",EDGE,"E22.5.13.0"),sQuery(id+"F0.wireOp",EDGE,"E22.9.13.0"),sQuery(id+"F0.wireOp",EDGE,"E22.13.13.0"),sQuery(id+"F0.wireOp",EDGE,"E22.17.13.0"),sQuery(id+"F0.wireOp",EDGE,"E22.3.14.0"),sQuery(id+"F0.wireOp",EDGE,"E22.5.14.0"),sQuery(id+"F0.wireOp",EDGE,"E22.9.14.0"),sQuery(id+"F0.wireOp",EDGE,"E22.13.14.0"),sQuery(id+"F0.wireOp",EDGE,"E22.17.14.0"),sQuery(id+"F0.wireOp",EDGE,"E22.3.15.0"),sQuery(id+"F0.wireOp",EDGE,"E22.5.15.0"),sQuery(id+"F0.wireOp",EDGE,"E22.9.15.0"),sQuery(id+"F0.wireOp",EDGE,"E22.13.15.0"),sQuery(id+"F0.wireOp",EDGE,"E22.17.15.0"),sQuery(id+"F0.wireOp",EDGE,"E22.3.16.0"),sQuery(id+"F0.wireOp",EDGE,"E22.5.16.0"),sQuery(id+"F0.wireOp",EDGE,"E22.9.16.0"),sQuery(id+"F0.wireOp",EDGE,"E22.13.16.0"),sQuery(id+"F0.wireOp",EDGE,"E22.17.16.0"),sQuery(id+"F0.wireOp",EDGE,"E22.3.17.0"),sQuery(id+"F0.wireOp",EDGE,"E22.5.17.0"),sQuery(id+"F0.wireOp",EDGE,"E22.9.17.0"),sQuery(id+"F0.wireOp",EDGE,"E22.13.17.0"),sQuery(id+"F0.wireOp",EDGE,"E22.17.17.0"),sQuery(id+"F0.wireOp",EDGE,"E22.3.18.0"),sQuery(id+"F0.wireOp",EDGE,"E22.5.18.0"),sQuery(id+"F0.wireOp",EDGE,"E22.9.18.0"),sQuery(id+"F0.wireOp",EDGE,"E22.13.18.0"),sQuery(id+"F0.wireOp",EDGE,"E22.17.18.0"),sQuery(id+"F0.wireOp",EDGE,"E22.3.19.0"),sQuery(id+"F0.wireOp",EDGE,"E22.5.19.0"),sQuery(id+"F0.wireOp",EDGE,"E22.9.19.0"),sQuery(id+"F0.wireOp",EDGE,"E22.13.19.0"),sQuery(id+"F0.wireOp",EDGE,"E22.17.19.0"),sQuery(id+"F0.wireOp",EDGE,"E23.trimOffspring"),sQuery(id+"F0.wireOp",EDGE,"E24.trimOffspring"),sQuery(id+"F0.wireOp",EDGE,"E25.trimOffspring"),sQuery(id+"F0.wireOp",EDGE,"E26.trimOffspring"),sQuery(id+"F0.wireOp",EDGE,"E27.trimOffspring"),sQuery(id+"F0.wireOp",EDGE,"E28.trimOffspring"),sQuery(id+"F0.wireOp",EDGE,"E29.trimOffspring"),sQuery(id+"F0.wireOp",EDGE,"E30.trimOffspring"),sQuery(id+"F0.wireOp",EDGE,"E31.trimOffspring"),sQuery(id+"F0.wireOp",EDGE,"E32.trimOffspring"),sQuery(id+"F0.wireOp",EDGE,"E33.trimOffspring"),sQuery(id+"F0.wireOp",EDGE,"E34.trimOffspring"),sQuery(id+"F0.wireOp",EDGE,"E35.trimOffspring"),sQuery(id+"F0.wireOp",EDGE,"E36.trimOffspring"),sQuery(id+"F0.wireOp",EDGE,"E37.trimOffspring"),sQuery(id+"F0.wireOp",EDGE,"E38.trimOffspring"),sQuery(id+"F0.wireOp",EDGE,"E39.trimOffspring"),sQuery(id+"F0.wireOp",EDGE,"E40.trimOffspring"),sQuery(id+"F0.wireOp",EDGE,"E41.trimOffspring")])],"isStart":true});
            var sketch = newSketch(context, id + "F4", { "sketchPlane" : qUnion([Q0])});
            skCircle(sketch, "E43", {"center": v(0, 0) * mm, "radius": 8 * mm});
            skSolve(sketch);
        }
        {
            var Q0;
            Q0=qSketchRegion(id+"F4",true);
            extrude(context, id + "F5", {"entities" : qUnion([Q0]), "operationType" : NewBodyOperationType.ADD, "depth" : 1.5 * mm});
        }
        {
            var Q0;
            Q0=makeQuery(id+"F5.opExtrude","CAP_FACE",FACE,{"disambiguationData":[OSD([sQuery(id+"F4.wireOp",EDGE,"E43")])],"isStart":false});
            var sketch = newSketch(context, id + "F6", { "sketchPlane" : qUnion([Q0])});
            skCircle(sketch, "E44", {"center": v(0, 0) * mm, "radius": 2.5 * mm});
            skSolve(sketch);
        }
        {
            var Q0;
            Q0=qSketchRegion(id+"F6",true);
            extrude(context, id + "F7", {"entities" : qUnion([Q0]), "operationType" : NewBodyOperationType.REMOVE, "endBound" : BoundingType.THROUGH_ALL, "oppositeDirection" : true, "depth" : 25 * mm});
        }
        {
            var Q0;
            Q0=qCreatedBy(makeId("Right.planeOp"),FACE);
            var sketch = newSketch(context, id + "F8", { "sketchPlane" : qUnion([Q0])});
            skCircle(sketch, "E45", {"center": v(0, 12) * mm, "radius": 1.5 * mm});
            skSolve(sketch);
        }
        {
            var Q0;
            Q0=qSketchRegion(id+"F8",true);
            extrude(context, id + "F9", {"entities" : qUnion([Q0]), "operationType" : NewBodyOperationType.REMOVE, "endBound" : BoundingType.THROUGH_ALL, "oppositeDirection" : true, "depth" : 25 * mm});
        }
    });
